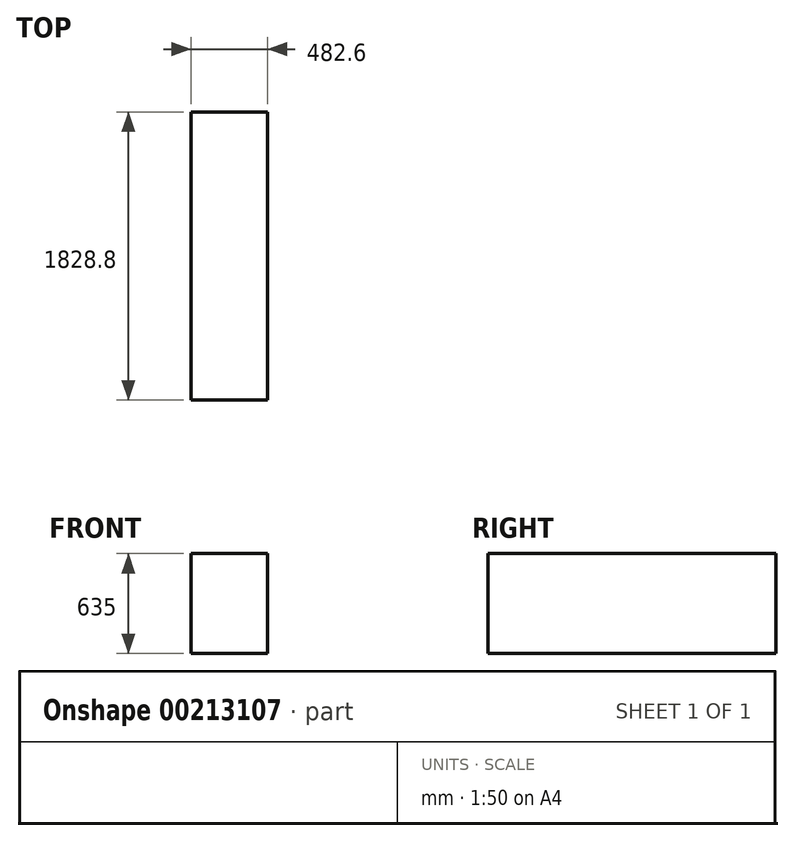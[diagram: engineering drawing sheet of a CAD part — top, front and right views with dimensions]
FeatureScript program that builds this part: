
annotation { "Feature Type Name" : "Feature", "Feature Type Description" : "" }
export const myFeature = defineFeature(function(context is Context, id is Id, definition is map)
    precondition{}
    {
        {
            var Q0;
            Q0=qCreatedBy(makeId("Front.planeOp"),FACE);
            var sketch = newSketch(context, id + "F0", { "sketchPlane" : qUnion([Q0])});
            skLineSegment(sketch, "E0.bottom", {"start": v(-33.05, 594.59) * mm, "end": v(449.55, 594.59) * mm});
            skLineSegment(sketch, "E0.top", {"start": v(-33.05, -40.41) * mm, "end": v(449.55, -40.41) * mm});
            skLineSegment(sketch, "E0.left", {"start": v(-33.05, 594.59) * mm, "end": v(-33.05, -40.41) * mm});
            skLineSegment(sketch, "E0.right", {"start": v(449.55, 594.59) * mm, "end": v(449.55, -40.41) * mm});
            skSolve(sketch);
        }
        {
            var Q0;
            Q0=makeQuery(id+"F0.imprint","IMPRINT",FACE,{"disambiguationData":[TD([[makeQuery(id+"F0.imprint","IMPRINT",EDGE,{"derivedFrom":sQuery(id+"F0.wireOp",EDGE,"E0.bottom")}),-1.0]])]});
            extrude(context, id + "F1", {"entities" : qUnion([Q0]), "depth" : 1828.8 * mm});
        }
    });
